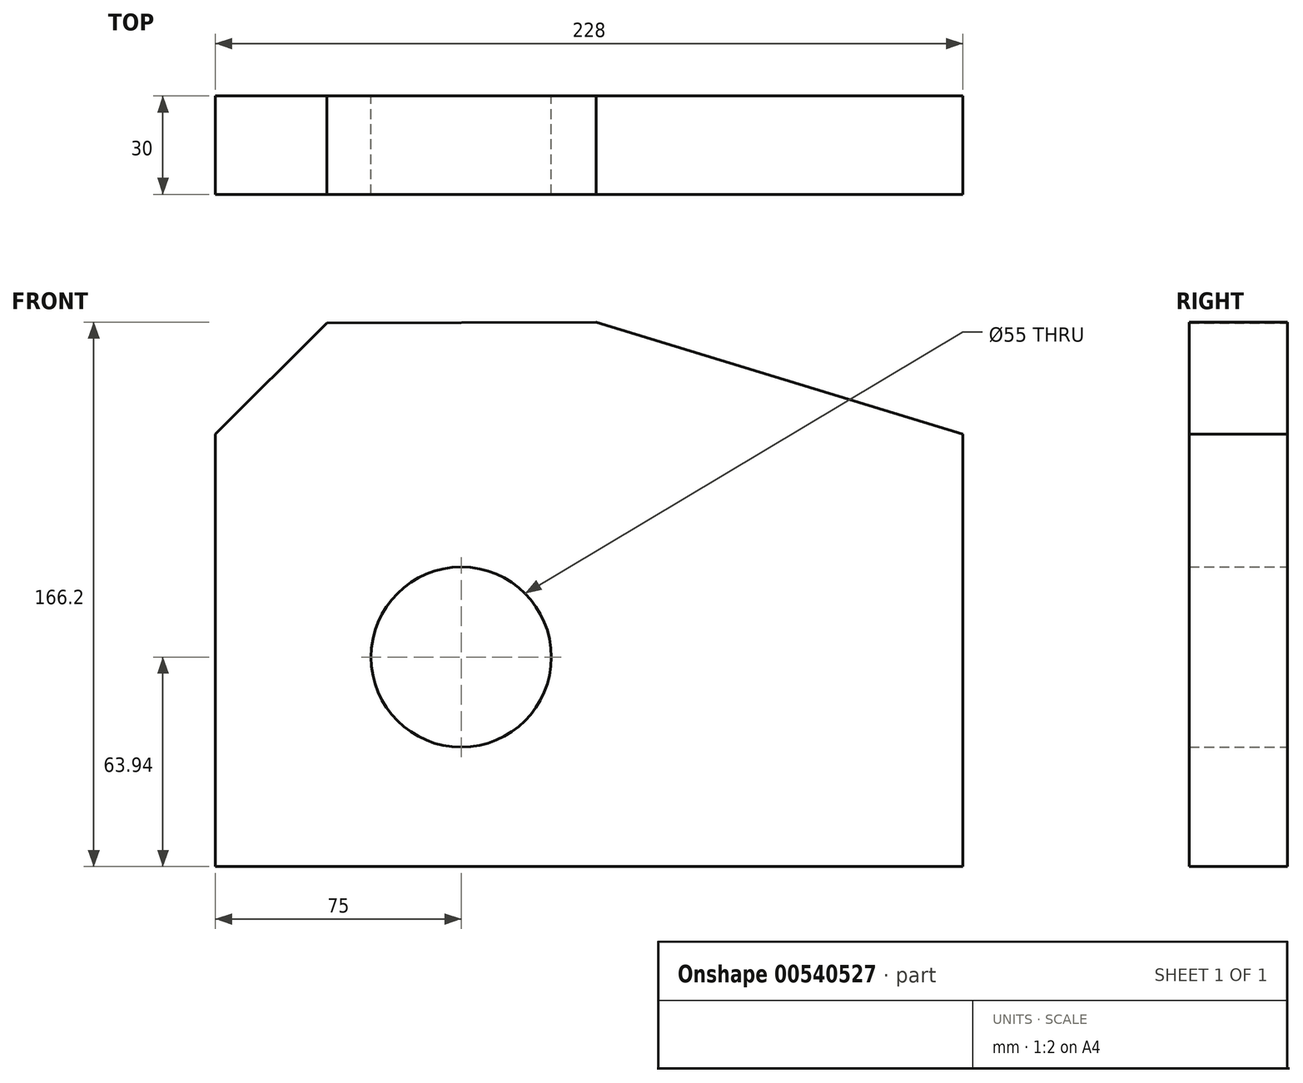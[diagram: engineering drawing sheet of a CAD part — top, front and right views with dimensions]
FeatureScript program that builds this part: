
annotation { "Feature Type Name" : "Feature", "Feature Type Description" : "" }
export const myFeature = defineFeature(function(context is Context, id is Id, definition is map)
    precondition{}
    {
        {
            var Q0;
            Q0=qCreatedBy(makeId("Front.planeOp"),FACE);
            var sketch = newSketch(context, id + "F0", { "sketchPlane" : qUnion([Q0])});
            skLineSegment(sketch, "E0", {"start": v(-75, 68.06) * mm, "end": v(-75, -63.94) * mm});
            skLineSegment(sketch, "E1", {"start": v(-75, -63.94) * mm, "end": v(153, -63.94) * mm});
            skLineSegment(sketch, "E2", {"start": v(153, -63.94) * mm, "end": v(153, 68.06) * mm});
            skLineSegment(sketch, "E3", {"start": v(-75, 68.06) * mm, "end": v(-41.06, 102) * mm});
            skLineSegment(sketch, "E4", {"start": v(153, 68.06) * mm, "end": v(41.11, 102.26) * mm});
            skLineSegment(sketch, "E5", {"start": v(-41.06, 102) * mm, "end": v(41.11, 102.26) * mm});
            skCircle(sketch, "E6", {"center": v(0, 0) * mm, "radius": 27.5 * mm});
            skSolve(sketch);
        }
        {
            var Q0;
            Q0 = qSketchRegion(id + "F0", true);
            extrude(context, id + "F1", {"entities" : qUnion([Q0]), "depth" : 30 * mm, "offsetDistance" : 25 * mm});
        }
    });
